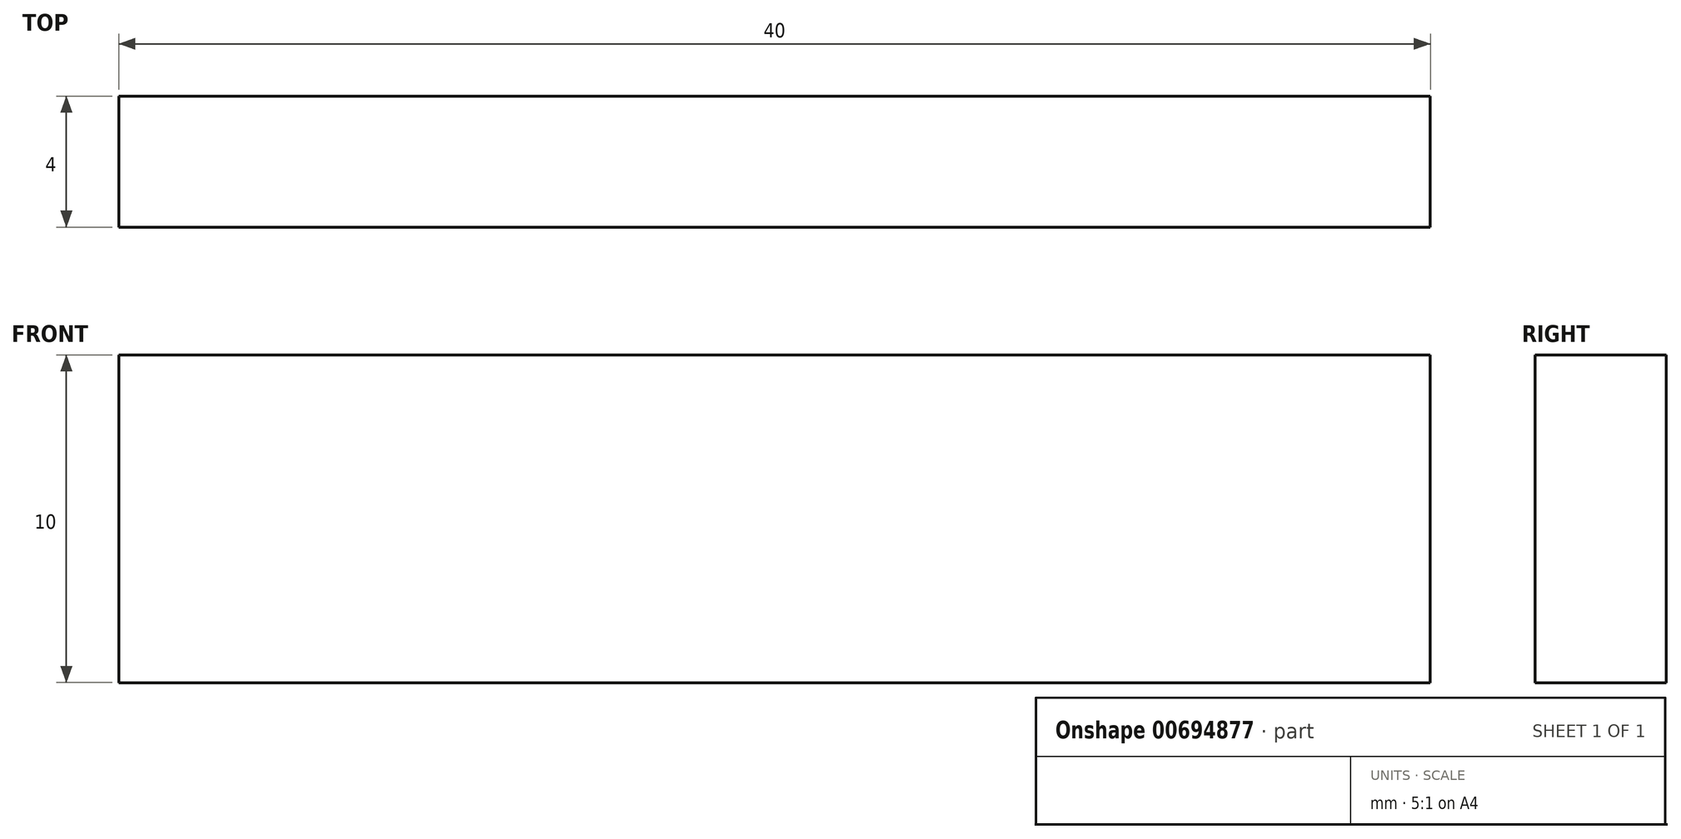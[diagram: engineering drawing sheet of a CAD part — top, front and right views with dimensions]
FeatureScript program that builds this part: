
annotation { "Feature Type Name" : "Feature", "Feature Type Description" : "" }
export const myFeature = defineFeature(function(context is Context, id is Id, definition is map)
    precondition{}
    {
        {
            var Q0;
            Q0=qCreatedBy(makeId("Front.planeOp"),FACE);
            var sketch = newSketch(context, id + "F0", { "sketchPlane" : qUnion([Q0])});
            skLineSegment(sketch, "E0.bottom", {"start": v(-14.3, 6.56) * mm, "end": v(25.7, 6.56) * mm});
            skLineSegment(sketch, "E0.top", {"start": v(-14.3, -3.44) * mm, "end": v(25.7, -3.44) * mm});
            skLineSegment(sketch, "E0.left", {"start": v(-14.3, 6.56) * mm, "end": v(-14.3, -3.44) * mm});
            skLineSegment(sketch, "E0.right", {"start": v(25.7, 6.56) * mm, "end": v(25.7, -3.44) * mm});
            skSolve(sketch);
        }
        {
            var Q0;
            Q0=makeQuery(id+"F0.imprint","IMPRINT",FACE,{"disambiguationData":[TD([[makeQuery(id+"F0.imprint","IMPRINT",EDGE,{"derivedFrom":sQuery(id+"F0.wireOp",EDGE,"E0.bottom")}),-1.0]])]});
            extrude(context, id + "F1", {"entities" : qUnion([Q0]), "depth" : 4 * mm, "offsetDistance" : 25 * mm});
        }
    });
